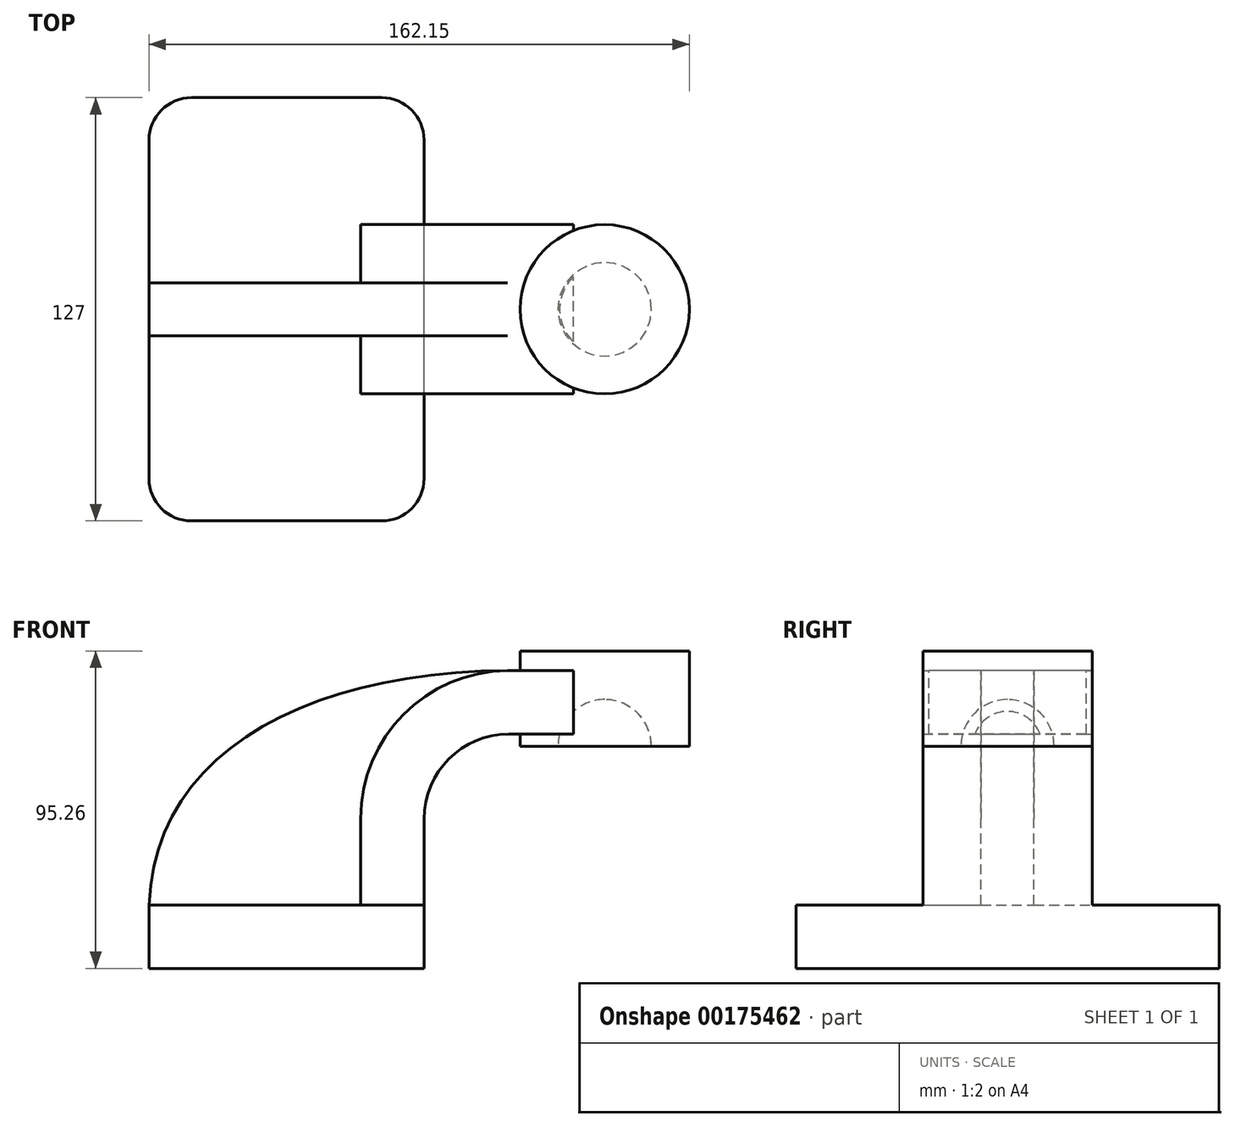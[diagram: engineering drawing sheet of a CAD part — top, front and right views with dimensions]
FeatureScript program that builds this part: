
annotation { "Feature Type Name" : "Feature", "Feature Type Description" : "" }
export const myFeature = defineFeature(function(context is Context, id is Id, definition is map)
    precondition{}
    {
        {
            var Q0;
            Q0=qCreatedBy(makeId("Front.planeOp"),FACE);
            var sketch = newSketch(context, id + "F0", { "sketchPlane" : qUnion([Q0])});
            skLineSegment(sketch, "E0.bottom", {"start": v(-41.28, 9.52) * mm, "end": v(41.27, 9.53) * mm});
            skLineSegment(sketch, "E0.top", {"start": v(-41.28, -9.53) * mm, "end": v(41.28, -9.53) * mm});
            skLineSegment(sketch, "E0.left", {"start": v(-41.28, 9.52) * mm, "end": v(-41.27, -9.53) * mm});
            skLineSegment(sketch, "E0.right", {"start": v(41.28, 9.53) * mm, "end": v(41.28, -9.52) * mm});
            skPoint(sketch, "E0.middle", {"position": v(0, 0) * mm});
            skLineSegment(sketch, "E1.bottom", {"start": v(70.07, 57.15) * mm, "end": v(120.87, 57.15) * mm});
            skLineSegment(sketch, "E1.top", {"start": v(70.07, 85.73) * mm, "end": v(120.87, 85.73) * mm});
            skLineSegment(sketch, "E1.left", {"start": v(70.07, 57.15) * mm, "end": v(70.07, 85.73) * mm});
            skLineSegment(sketch, "E1.right", {"start": v(120.87, 57.15) * mm, "end": v(120.87, 85.73) * mm});
            skPoint(sketch, "E1.middle", {"position": v(95.47, 71.44) * mm});
            skLineSegment(sketch, "E2", {"start": v(41.27, 9.53) * mm, "end": v(41.27, 35.37) * mm});
            skArc(sketch, "E3", {"start": v(41.27, 35.37) * mm, "mid": v(48.71, 53.33) * mm, "end": v(66.67, 60.77) * mm});
            skLineSegment(sketch, "E4", {"start": v(66.67, 60.77) * mm, "end": v(86.14, 60.77) * mm});
            skLineSegment(sketch, "E5.0", {"start": v(66.67, 79.82) * mm, "end": v(86.14, 79.82) * mm});
            skArc(sketch, "E5.1", {"start": v(22.22, 35.37) * mm, "mid": v(35.24, 66.8) * mm, "end": v(66.67, 79.82) * mm});
            skLineSegment(sketch, "E5.2", {"start": v(22.22, 9.53) * mm, "end": v(22.22, 35.37) * mm});
            skLineSegment(sketch, "E6", {"start": v(86.14, 60.77) * mm, "end": v(86.14, 79.82) * mm});
            skFitSpline(sketch, "E7", {"points": [v(-41.28, 9.52) * mm, v(66.67, 79.82) * mm], "startDerivative": vector(4.87, 135.98) * mm, "endDerivative": vector(183.38, 0.67) * mm});
            skLineSegment(sketch, "E8", {"start": v(95.47, 71.44) * mm, "end": v(95.47, 85.73) * mm});
            skLineSegment(sketch, "E9", {"start": v(95.47, 85.73) * mm, "end": v(95.47, 57.15) * mm});
            skArc(sketch, "E10", {"start": v(109.46, 57.15) * mm, "mid": v(105.36, 67.05) * mm, "end": v(95.47, 71.15) * mm});
            skSolve(sketch);
        }
        {
            var Q0;
            Q0=makeQuery(id+"F0.imprint","IMPRINT",FACE,{"disambiguationData":[TD([[makeQuery(id+"F0.imprint","IMPRINT",EDGE,{"derivedFrom":sQuery(id+"F0.wireOp",EDGE,"E0.top")}),1.0]])]});
            extrude(context, id + "F1", {"entities" : qUnion([Q0]), "endBound" : BoundingType.SYMMETRIC, "depth" : 127 * mm});
        }
        {
            var Q0;
            {var subQ1=sQuery(id+"F0.wireOp",EDGE,"E2");Q0=makeQuery(id+"F0.imprint","IMPRINT",FACE,{"disambiguationData":[TD([[makeQuery(id+"F0.imprint","IMPRINT",EDGE,{"derivedFrom":subQ1}),1.0]])]});}
            var Q1;
            {var subQ5=sQuery(id+"F0.wireOp",EDGE,"E6");Q1=makeQuery(id+"F0.imprint","IMPRINT",FACE,{"disambiguationData":[TD([[makeQuery(id+"F0.imprint","IMPRINT",EDGE,{"derivedFrom":subQ5}),1.0]])]});}
            extrude(context, id + "F2", {"entities" : qUnion([Q0, Q1]), "operationType" : NewBodyOperationType.ADD, "endBound" : BoundingType.SYMMETRIC, "depth" : 50.8 * mm});
        }
        {
            var Q0;
            {var subQ3=sQuery(id+"F0.wireOp",EDGE,"E5.2");Q0=makeQuery(id+"F0.imprint","IMPRINT",FACE,{"disambiguationData":[TD([[makeQuery(id+"F0.imprint","IMPRINT",EDGE,{"derivedFrom":subQ3}),1.0]])]});}
            extrude(context, id + "F3", {"entities" : qUnion([Q0]), "operationType" : NewBodyOperationType.ADD, "endBound" : BoundingType.SYMMETRIC, "depth" : 15.88 * mm});
        }
        {
            var Q0;
            {var subQ0=sQuery(id+"F0.wireOp",EDGE,"E1.right");Q0=makeQuery(id+"F0.imprint","IMPRINT",FACE,{"disambiguationData":[TD([[makeQuery(id+"F0.imprint","IMPRINT",EDGE,{"derivedFrom":subQ0}),1.0]])]});}
            var Q1;
            Q1=sQuery(id+"F0.wireOp",EDGE,"E9");
            revolve(context, id + "F4", {"operationType" : NewBodyOperationType.ADD, "entities" : qUnion([Q0]), "axis" : qUnion([Q1]), "revolveType" : RevolveType.FULL});
        }
        {
            var Q0;
            Q0=makeQuery(id+"F1.opExtrude","CAP_EDGE",EDGE,{"disambiguationData":[OSD([sQuery(id+"F0.wireOp",EDGE,"E0.left")])],"isStart":false});
            var Q1;
            Q1=makeQuery(id+"F1.opExtrude","CAP_EDGE",EDGE,{"disambiguationData":[OSD([sQuery(id+"F0.wireOp",EDGE,"E0.right")])],"isStart":false});
            var Q2;
            Q2=makeQuery(id+"F1.opExtrude","CAP_EDGE",EDGE,{"disambiguationData":[OSD([sQuery(id+"F0.wireOp",EDGE,"E0.right")])],"isStart":true});
            var Q3;
            Q3=makeQuery(id+"F1.opExtrude","CAP_EDGE",EDGE,{"disambiguationData":[OSD([sQuery(id+"F0.wireOp",EDGE,"E0.left")])],"isStart":true});
            fillet(context, id + "F5", {"entities" : qUnion([Q0, Q1, Q2, Q3]), "radius" : 12.7 * mm, "tangentPropagation" : true, "allowEdgeOverflow" : false});
        }
    });
